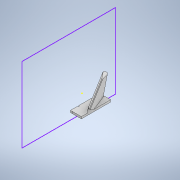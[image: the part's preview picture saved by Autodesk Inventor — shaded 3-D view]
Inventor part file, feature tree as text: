
AUTODESK INVENTOR PART (.ipt)
format: ipt  version: 2020 (Build 240168000, 168)  size: 323,584 bytes
history: native  units: mm
features: extrude x12, sketch x12, projected_geometry x4, chamfer x2, plane x1, fillet x1
ambient origin geometry x8: Origin, YZ Plane, XZ Plane, XY Plane, X Axis, Y Axis, Z Axis, Center Point
bodies: Solid1 (feature_tree)
feature tree (32):
  extrude  "Extrusion1"  Depth=3.0mm
  sketch  "Sketch2"  dims[d4=12.042772mm d6=3.0mm d7=0.0mm]
  extrude  "Extrusion2"  Depth=3.0mm TaperAngle=0.0deg
  plane  "Work Plane1"
  sketch  "Sketch4"  dims[d14=84.5mm d15=0.0mm d16=84.5mm d17=0.0mm]
  extrude  "Extrusion5"  Depth=50.982799mm
  extrude  "Extrusion6"  Depth=84.5mm TaperAngle=0.0deg
  extrude  "Extrusion7"  Depth=4.0mm TaperAngle=0.0deg
  extrude  "Extrusion8"  Depth=159.75mm TaperAngle=0.0deg
  extrude  "Extrusion9"  Depth=159.75mm TaperAngle=0.0deg
  sketch  "Sketch9"  dims[d30=2.8mm d31=4.85mm d32=15.25mm d33=45.0deg]
  extrude  "Extrusion10"  Depth=2.8mm TaperAngle=45.0deg
  extrude  "Extrusion11"  Depth=16.5mm TaperAngle=0.0deg
  extrude  "Extrusion12"  [1 undecoded]
  fillet  "Fillet1"  [1 undecoded]
  chamfer  "Chamfer1"  [1 undecoded]
  chamfer  "Chamfer2"  [1 undecoded]
  sketch  "Sketch13"
  extrude  "Extrusion13"  [1 undecoded]
  extrude  "Extrusion14"  [1 undecoded]
  sketch  "Sketch1"  dims[d0=3.0mm d1=0.0mm d2=65.0mm]
  sketch  "Sketch3"  dims[d8=45.0deg d13=50.982799mm]
  projected_geometry  "Projected Loop1"
  projected_geometry  "Projected Loop2"
  sketch  "Sketch5"  dims[d18=211.75mm d19=0.0mm d20=4.0mm d21=0.0mm]
  sketch  "Sketch7"  dims[d22=4.0mm d23=0.0mm d24=159.75mm d25=0.0mm]
  projected_geometry  "Projected Loop5"
  sketch  "Sketch8"  dims[d26=159.75mm d27=0.0mm d28=159.75mm d29=0.0mm]
  projected_geometry  "Projected Loop6"
  sketch  "Sketch10"  dims[d34=4.85mm d35=15.25mm d36=45.0deg d43=16.5mm d44=0.0mm]
  sketch  "Sketch11"  dims[d45=48.25mm d46=0.0mm]
  sketch  "Sketch12"
note: 6 required parameter values undecoded (feature->parameter linkage not recoverable at this tier; creation-order binding heuristic only, values carry confidence <= 0.55)
